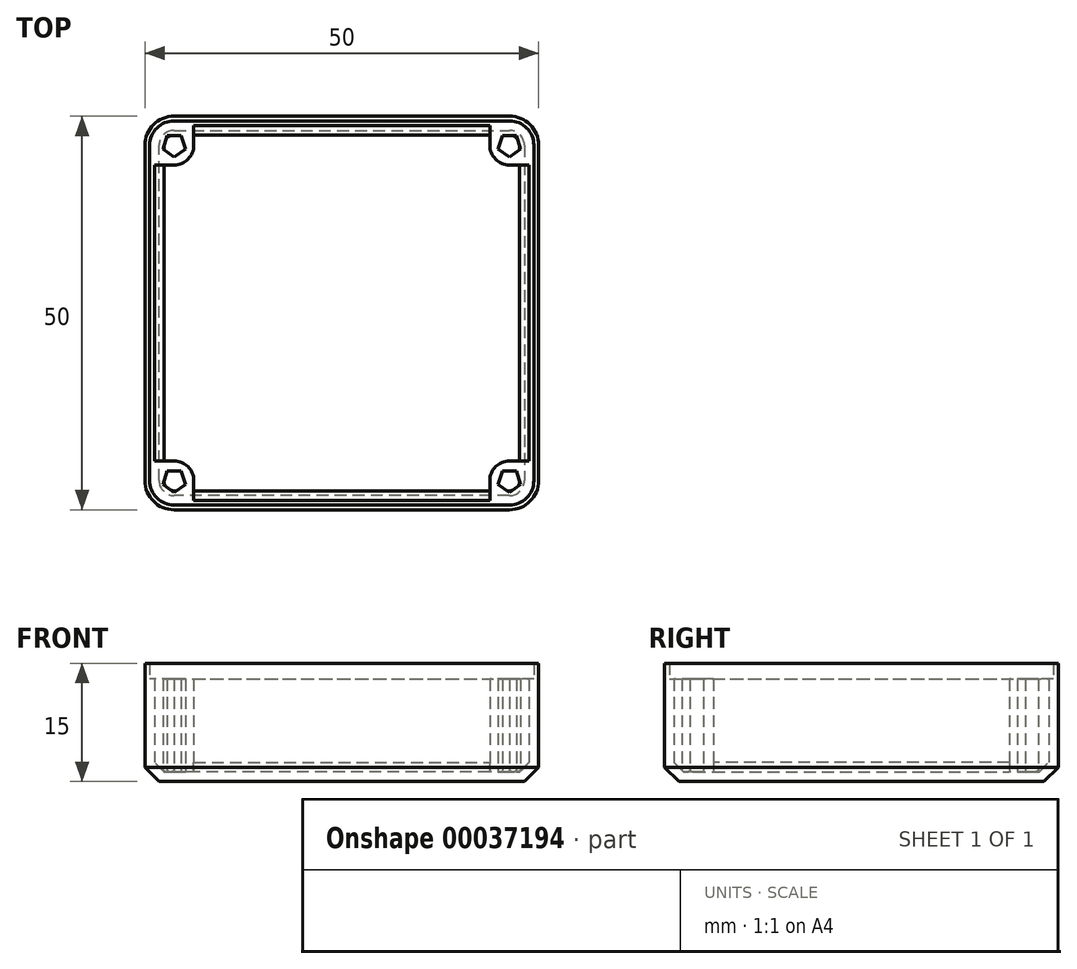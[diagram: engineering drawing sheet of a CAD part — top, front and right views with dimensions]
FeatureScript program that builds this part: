
annotation { "Feature Type Name" : "Feature", "Feature Type Description" : "" }
export const myFeature = defineFeature(function(context is Context, id is Id, definition is map)
    precondition{}
    {
        {
            assignVariable(context, id + "F0", {"name" : "Hoehe", "anyValue" : 15 * mm});
        }
        {
            assignVariable(context, id + "F1", {"name" : "Wandstaerke", "anyValue" : 1.2 * mm});
        }
        {
            var Q0;
            Q0=qCreatedBy(makeId("Top.planeOp"),FACE);
            var sketch = newSketch(context, id + "F2", { "sketchPlane" : qUnion([Q0])});
            skLineSegment(sketch, "E0.rect.bottom", {"start": v(-21.3, -25) * mm, "end": v(21.3, -25) * mm});
            skLineSegment(sketch, "E0.rect.top", {"start": v(-21.3, 25) * mm, "end": v(21.3, 25) * mm});
            skLineSegment(sketch, "E0.rect.left", {"start": v(-25, -21.3) * mm, "end": v(-25, 21.3) * mm});
            skLineSegment(sketch, "E0.rect.right", {"start": v(25, -21.3) * mm, "end": v(25, 21.3) * mm});
            skPoint(sketch, "E0.rect.middle", {"position": v(0, 0) * mm});
            skPoint(sketch, "E1.visualSharp", {"position": v(-25, 25) * mm});
            skArc(sketch, "E1.filletArc", {"start": v(-21.3, 25) * mm, "mid": v(-23.92, 23.92) * mm, "end": v(-25, 21.3) * mm});
            skPoint(sketch, "E2.visualSharp", {"position": v(-25, -25) * mm});
            skArc(sketch, "E2.filletArc", {"start": v(-25, -21.3) * mm, "mid": v(-23.92, -23.92) * mm, "end": v(-21.3, -25) * mm});
            skPoint(sketch, "E3.visualSharp", {"position": v(25, -25) * mm});
            skArc(sketch, "E3.filletArc", {"start": v(21.3, -25) * mm, "mid": v(23.92, -23.92) * mm, "end": v(25, -21.3) * mm});
            skPoint(sketch, "E4.visualSharp", {"position": v(25, 25) * mm});
            skArc(sketch, "E4.filletArc", {"start": v(25, 21.3) * mm, "mid": v(23.92, 23.92) * mm, "end": v(21.3, 25) * mm});
            skSolve(sketch);
        }
        {
            var Q0;
            Q0 = qSketchRegion(id + "F2", true);
            var Q1;
            Q1 = qSketchRegion(id + "F5", true);
            extrude(context, id + "F3", {"entities" : qUnion([Q0, Q1]), "depth" : getVariable(context, 'Hoehe') - 2 * mm});
        }
        {
            var Q0;
            Q0=makeQuery(id+"F3.opExtrude","CAP_FACE",FACE,{"disambiguationData":[OSD([sQuery(id+"F2.wireOp",EDGE,"E0.rect.bottom"),sQuery(id+"F2.wireOp",EDGE,"E0.rect.top"),sQuery(id+"F2.wireOp",EDGE,"E0.rect.left"),sQuery(id+"F2.wireOp",EDGE,"E0.rect.right")])],"isStart":false});
            shell(context, id + "F4", {"entities" : qUnion([Q0]), "thickness" : getVariable(context, 'Wandstaerke')});
        }
        {
            var Q0;
            Q0=makeQuery(id+"F4.opShell","OFFSET_FACE",FACE,{"disambiguationData":[OSD([sQuery(id+"F2.wireOp",EDGE,"E0.rect.bottom"),sQuery(id+"F2.wireOp",EDGE,"E0.rect.top"),sQuery(id+"F2.wireOp",EDGE,"E0.rect.left"),sQuery(id+"F2.wireOp",EDGE,"E0.rect.right"),sQuery(id+"F2.wireOp",EDGE,"E1.filletArc"),sQuery(id+"F2.wireOp",EDGE,"E2.filletArc"),sQuery(id+"F2.wireOp",EDGE,"E3.filletArc"),sQuery(id+"F2.wireOp",EDGE,"E4.filletArc")])]});
            var sketch = newSketch(context, id + "F5", { "sketchPlane" : qUnion([Q0])});
            skArc(sketch, "E5", {"start": v(-21.3, 18.8) * mm, "mid": v(-19.53, 19.53) * mm, "end": v(-18.8, 21.3) * mm});
            skLineSegment(sketch, "E6", {"start": v(-21.3, 18.8) * mm, "end": v(-23.8, 18.8) * mm});
            skLineSegment(sketch, "E7", {"start": v(-18.8, 21.3) * mm, "end": v(-18.8, 23.8) * mm});
            skCircle(sketch, "E8.cCircle", {"center": v(-21.3, 21.3) * mm, "radius": 1.5 * mm, "construction": true});
            skLineSegment(sketch, "E8.0", {"start": v(-21.3, 19.8) * mm, "end": v(-22.73, 20.84) * mm});
            skLineSegment(sketch, "E8.1", {"start": v(-22.73, 20.84) * mm, "end": v(-22.18, 22.51) * mm});
            skLineSegment(sketch, "E8.2", {"start": v(-22.18, 22.51) * mm, "end": v(-20.42, 22.51) * mm});
            skLineSegment(sketch, "E8.3", {"start": v(-20.42, 22.51) * mm, "end": v(-19.87, 20.84) * mm});
            skLineSegment(sketch, "E8.4", {"start": v(-19.87, 20.84) * mm, "end": v(-21.3, 19.8) * mm});
            skLineSegment(sketch, "E9", {"start": v(18.8, 21.3) * mm, "end": v(18.8, 23.8) * mm});
            skCircle(sketch, "E10.cCircle", {"center": v(21.3, 21.3) * mm, "radius": 1.5 * mm, "construction": true});
            skLineSegment(sketch, "E10.2", {"start": v(20.42, 22.51) * mm, "end": v(22.18, 22.51) * mm});
            skLineSegment(sketch, "E10.1", {"start": v(19.87, 20.84) * mm, "end": v(20.42, 22.51) * mm});
            skLineSegment(sketch, "E11", {"start": v(21.3, 18.8) * mm, "end": v(23.8, 18.8) * mm});
            skArc(sketch, "E12", {"start": v(18.8, 21.3) * mm, "mid": v(19.53, 19.53) * mm, "end": v(21.3, 18.8) * mm});
            skLineSegment(sketch, "E10.3", {"start": v(22.18, 22.51) * mm, "end": v(22.73, 20.84) * mm});
            skLineSegment(sketch, "E10.0", {"start": v(21.3, 19.8) * mm, "end": v(19.87, 20.84) * mm});
            skLineSegment(sketch, "E10.4", {"start": v(22.73, 20.84) * mm, "end": v(21.3, 19.8) * mm});
            skCircle(sketch, "E13.cCircle", {"center": v(21.3, -21.3) * mm, "radius": 1.5 * mm, "construction": true});
            skLineSegment(sketch, "E14", {"start": v(18.8, -21.3) * mm, "end": v(18.8, -23.8) * mm});
            skLineSegment(sketch, "E15", {"start": v(21.3, -18.8) * mm, "end": v(23.8, -18.8) * mm});
            skArc(sketch, "E16", {"start": v(21.3, -18.8) * mm, "mid": v(19.53, -19.53) * mm, "end": v(18.8, -21.3) * mm});
            skLineSegment(sketch, "E13.2", {"start": v(20.42, -20.09) * mm, "end": v(22.18, -20.09) * mm});
            skLineSegment(sketch, "E13.4", {"start": v(22.73, -21.76) * mm, "end": v(21.3, -22.8) * mm});
            skLineSegment(sketch, "E13.0", {"start": v(21.3, -22.8) * mm, "end": v(19.87, -21.76) * mm});
            skLineSegment(sketch, "E13.3", {"start": v(22.18, -20.09) * mm, "end": v(22.73, -21.76) * mm});
            skLineSegment(sketch, "E13.1", {"start": v(19.87, -21.76) * mm, "end": v(20.42, -20.09) * mm});
            skCircle(sketch, "E17.cCircle", {"center": v(-21.3, -21.3) * mm, "radius": 1.5 * mm, "construction": true});
            skLineSegment(sketch, "E18", {"start": v(-21.3, -18.8) * mm, "end": v(-23.8, -18.8) * mm});
            skLineSegment(sketch, "E19", {"start": v(-18.8, -21.3) * mm, "end": v(-18.8, -23.8) * mm});
            skArc(sketch, "E20", {"start": v(-18.8, -21.3) * mm, "mid": v(-19.53, -19.53) * mm, "end": v(-21.3, -18.8) * mm});
            skLineSegment(sketch, "E17.2", {"start": v(-22.18, -20.09) * mm, "end": v(-20.42, -20.09) * mm});
            skLineSegment(sketch, "E17.4", {"start": v(-19.87, -21.76) * mm, "end": v(-21.3, -22.8) * mm});
            skLineSegment(sketch, "E17.0", {"start": v(-21.3, -22.8) * mm, "end": v(-22.73, -21.76) * mm});
            skLineSegment(sketch, "E17.3", {"start": v(-20.42, -20.09) * mm, "end": v(-19.87, -21.76) * mm});
            skLineSegment(sketch, "E17.1", {"start": v(-22.73, -21.76) * mm, "end": v(-22.18, -20.09) * mm});
            skSolve(sketch);
        }
        {
            var Q0;
            Q0=makeQuery(id+"F3.opExtrude","CAP_FACE",FACE,{"disambiguationData":[OSD([sQuery(id+"F2.wireOp",EDGE,"E0.rect.bottom"),sQuery(id+"F2.wireOp",EDGE,"E0.rect.top"),sQuery(id+"F2.wireOp",EDGE,"E0.rect.left"),sQuery(id+"F2.wireOp",EDGE,"E0.rect.right")])],"isStart":true});
            chamfer(context, id + "F6", {"entities" : qUnion([Q0]), "width" : getVariable(context, 'Wandstaerke') * 1.5, "tangentPropagation" : true});
        }
        {
            var Q0;
            {var subQ0=sQuery(id+"F2.wireOp",EDGE,"E0.rect.bottom");var subQ1=sQuery(id+"F2.wireOp",EDGE,"E0.rect.top");var subQ2=sQuery(id+"F2.wireOp",EDGE,"E0.rect.left");var subQ3=sQuery(id+"F2.wireOp",EDGE,"E0.rect.right");Q0=makeQuery(id+"F4ahzGhQXwVZ54h_1.boolean.opBoolean","SPLIT",FACE,{"disambiguationData":[TD([makeQuery(id+"F4.opShell","OFFSET_FACE",FACE,{"disambiguationData":[OSD([subQ0])]})])],"derivedFrom":makeQuery(id+"F4.opShell","OFFSET_FACE",FACE,{"disambiguationData":[OSD([subQ0,subQ1,subQ2,subQ3])]})});}
            chamfer(context, id + "F7", {"entities" : qUnion([Q0]), "width" : getVariable(context, 'Wandstaerke'), "tangentPropagation" : true});
        }
        {
            var Q0;
            Q0=makeQuery(id+"F5.imprint","IMPRINT",FACE,{"disambiguationData":[TD([[makeQuery(id+"F5.imprint","IMPRINT",EDGE,{"derivedFrom":sQuery(id+"F5.wireOp",EDGE,"E5")}),1.0]])]});
            var Q1;
            {var subQ5=sQuery(id+"F5.wireOp",EDGE,"E18");Q1=makeQuery(id+"F5.imprint","IMPRINT",FACE,{"disambiguationData":[TD([[makeQuery(id+"F5.imprint","IMPRINT",EDGE,{"derivedFrom":subQ5}),1.0]])]});}
            var Q2;
            {var subQ4=sQuery(id+"F5.wireOp",EDGE,"E9");Q2=makeQuery(id+"F5.imprint","IMPRINT",FACE,{"disambiguationData":[TD([[makeQuery(id+"F5.imprint","IMPRINT",EDGE,{"derivedFrom":subQ4}),-1.0]])]});}
            var Q3;
            {var subQ4=sQuery(id+"F5.wireOp",EDGE,"E14");Q3=makeQuery(id+"F5.imprint","IMPRINT",FACE,{"disambiguationData":[TD([[makeQuery(id+"F5.imprint","IMPRINT",EDGE,{"derivedFrom":subQ4}),1.0]])]});}
            var Q4;
            Q4=makeQuery(id+"F3.opExtrude","CAP_FACE",FACE,{"disambiguationData":[OSD([sQuery(id+"F2.wireOp",EDGE,"E0.rect.bottom"),sQuery(id+"F2.wireOp",EDGE,"E0.rect.top"),sQuery(id+"F2.wireOp",EDGE,"E0.rect.left"),sQuery(id+"F2.wireOp",EDGE,"E0.rect.right"),sQuery(id+"F2.wireOp",EDGE,"E1.filletArc"),sQuery(id+"F2.wireOp",EDGE,"E2.filletArc"),sQuery(id+"F2.wireOp",EDGE,"E3.filletArc"),sQuery(id+"F2.wireOp",EDGE,"E4.filletArc")])],"isStart":false});
            extrude(context, id + "F8", {"entities" : qUnion([Q0, Q1, Q2, Q3]), "operationType" : NewBodyOperationType.ADD, "endBound" : BoundingType.UP_TO_SURFACE, "endBoundEntityFace" : qUnion([Q4]), "depth" : 25 * mm});
        }
        {
            var Q0;
            {var subQ0=sQuery(id+"F2.wireOp",EDGE,"E2.filletArc");var subQ1=sQuery(id+"F2.wireOp",EDGE,"E0.rect.left");var subQ2=sQuery(id+"F2.wireOp",EDGE,"E0.rect.bottom");var subQ3=sQuery(id+"F2.wireOp",EDGE,"E3.filletArc");var subQ4=sQuery(id+"F2.wireOp",EDGE,"E0.rect.right");var subQ5=sQuery(id+"F2.wireOp",EDGE,"E4.filletArc");var subQ6=sQuery(id+"F2.wireOp",EDGE,"E0.rect.top");var subQ7=sQuery(id+"F2.wireOp",EDGE,"E1.filletArc");Q0=makeQuery(id+"F8.boolean.opBoolean","MERGE",FACE,{"derivedFrom":[makeQuery(id+"F3.opExtrude","CAP_FACE",FACE,{"disambiguationData":[OSD([subQ2,subQ6,subQ1,subQ4,subQ7,subQ0,subQ3,subQ5])],"isStart":false}),makeQuery(id+"F8.opExtrude","CAP_FACE",FACE,{"disambiguationData":[OSD([subQ6,subQ1,subQ7,sQuery(id+"F5.wireOp",EDGE,"E5"),sQuery(id+"F5.wireOp",EDGE,"E6"),sQuery(id+"F5.wireOp",EDGE,"E7"),sQuery(id+"F5.wireOp",EDGE,"E8.0"),sQuery(id+"F5.wireOp",EDGE,"E8.1"),sQuery(id+"F5.wireOp",EDGE,"E8.2"),sQuery(id+"F5.wireOp",EDGE,"E8.3"),sQuery(id+"F5.wireOp",EDGE,"E8.4")])],"isStart":false}),makeQuery(id+"F8.opExtrude","CAP_FACE",FACE,{"disambiguationData":[OSD([subQ6,subQ4,subQ5,sQuery(id+"F5.wireOp",EDGE,"E9"),sQuery(id+"F5.wireOp",EDGE,"E10.2"),sQuery(id+"F5.wireOp",EDGE,"E10.1"),sQuery(id+"F5.wireOp",EDGE,"E11"),sQuery(id+"F5.wireOp",EDGE,"E12"),sQuery(id+"F5.wireOp",EDGE,"E10.3"),sQuery(id+"F5.wireOp",EDGE,"E10.0"),sQuery(id+"F5.wireOp",EDGE,"E10.4")])],"isStart":false}),makeQuery(id+"F8.opExtrude","CAP_FACE",FACE,{"disambiguationData":[OSD([subQ2,subQ4,subQ3,sQuery(id+"F5.wireOp",EDGE,"E14"),sQuery(id+"F5.wireOp",EDGE,"E15"),sQuery(id+"F5.wireOp",EDGE,"E16"),sQuery(id+"F5.wireOp",EDGE,"E13.2"),sQuery(id+"F5.wireOp",EDGE,"E13.4"),sQuery(id+"F5.wireOp",EDGE,"E13.0"),sQuery(id+"F5.wireOp",EDGE,"E13.3"),sQuery(id+"F5.wireOp",EDGE,"E13.1")])],"isStart":false}),makeQuery(id+"F8.opExtrude","CAP_FACE",FACE,{"disambiguationData":[OSD([subQ2,subQ1,subQ0,sQuery(id+"F5.wireOp",EDGE,"E18"),sQuery(id+"F5.wireOp",EDGE,"E19"),sQuery(id+"F5.wireOp",EDGE,"E20"),sQuery(id+"F5.wireOp",EDGE,"E17.2"),sQuery(id+"F5.wireOp",EDGE,"E17.4"),sQuery(id+"F5.wireOp",EDGE,"E17.0"),sQuery(id+"F5.wireOp",EDGE,"E17.3"),sQuery(id+"F5.wireOp",EDGE,"E17.1")])],"isStart":false})]});}
            var sketch = newSketch(context, id + "F9", { "sketchPlane" : qUnion([Q0])});
            skLineSegment(sketch, "E21.0", {"start": v(-21.3, 24.4) * mm, "end": v(21.3, 24.4) * mm});
            skArc(sketch, "E21.1", {"start": v(24.4, 21.3) * mm, "mid": v(23.5, 23.5) * mm, "end": v(21.3, 24.4) * mm});
            skArc(sketch, "E21.2", {"start": v(-21.3, 24.4) * mm, "mid": v(-23.5, 23.5) * mm, "end": v(-24.4, 21.3) * mm});
            skLineSegment(sketch, "E21.3", {"start": v(24.4, -21.3) * mm, "end": v(24.4, 21.3) * mm});
            skLineSegment(sketch, "E21.4", {"start": v(-24.4, -21.3) * mm, "end": v(-24.4, 21.3) * mm});
            skArc(sketch, "E21.5", {"start": v(-24.4, -21.3) * mm, "mid": v(-23.5, -23.5) * mm, "end": v(-21.3, -24.4) * mm});
            skLineSegment(sketch, "E21.6", {"start": v(-21.3, -24.4) * mm, "end": v(21.3, -24.4) * mm});
            skArc(sketch, "E21.7", {"start": v(21.3, -24.4) * mm, "mid": v(23.5, -23.5) * mm, "end": v(24.4, -21.3) * mm});
            skSolve(sketch);
        }
        {
            var Q0;
            Q0=makeQuery(id+"F9.imprint","IMPRINT",FACE,{"disambiguationData":[TD([[makeQuery(id+"F9.imprint","IMPRINT",EDGE,{"derivedFrom":sQuery(id+"F9.wireOp",EDGE,"E21.0")}),1.0]])]});
            extrude(context, id + "F10", {"entities" : qUnion([Q0]), "operationType" : NewBodyOperationType.ADD, "depth" : 2 * mm});
        }
    });
